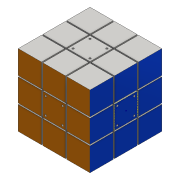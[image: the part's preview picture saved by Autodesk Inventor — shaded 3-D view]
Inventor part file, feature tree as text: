
AUTODESK INVENTOR PART (.ipt)
format: ipt  version: 2016 (Build 200138000, 138)  size: 400,384 bytes
history: native  units: mm
features: sketch x8, extrude x7, mirror x5, pattern_circular x5, plane x4, other x1, projected_geometry x1
ambient origin geometry x8: Origin, YZ Plane, XZ Plane, XY Plane, X Axis, Y Axis, Z Axis, Center Point
bodies: 实体1 (feature_tree)
feature tree (31):
  extrude  "拉伸1"  Depth=57.0mm TaperAngle=0.0deg
  extrude  "拉伸2"  Depth=1.0mm
  mirror  "镜像1"
  extrude  "拉伸3"  Depth=18.5mm
  plane  "工作平面1"
  mirror  "镜像2"
  pattern_circular  "环形阵列1"  Count=4 Angle=360.0deg
  pattern_circular  "环形阵列2"  Count=4 Angle=360.0deg
  extrude  "拉伸4"  Depth=1.0mm TaperAngle=360.0deg
  pattern_circular  "环形阵列3"  [2 undecoded]
  extrude  "拉伸5"  Depth=1.0mm
  mirror  "镜像3"
  extrude  "拉伸6"  Depth=18.5mm
  mirror  "镜像4"
  extrude  "拉伸7"  Depth=4.0mm TaperAngle=0.0deg
  mirror  "镜像5"
  pattern_circular  "环形阵列4"  [2 undecoded]
  sketch  "草图8"  dims[d23=1.0mm d24=18.5mm d25=1.0mm d26=18.5mm d27=60.0mm d28=0.0mm d29=1.0mm d30=0.0mm d31=19.0mm d32=1.5mm d33=1.5mm d34=4.0mm d35=0.0mm d36=40.0mm d37=360.0deg d39=40.0mm d40=360.0deg]
  other  "工作轴4"
  pattern_circular  "环形阵列5"  [2 undecoded]
  sketch  "草图1"  dims[d0=57.0mm d1=57.0mm d2=0.0mm]
  sketch  "草图2"  dims[d3=18.5mm d4=1.0mm]
  projected_geometry  "投影回路1"
  sketch  "草图3"  dims[d5=1.0mm d6=18.5mm]
  sketch  "草图4"  dims[d7=1.0mm d8=0.0mm]
  sketch  "草图5"  dims[d9=1.0mm d10=0.0mm]
  plane  "工作平面2"
  sketch  "草图6"  dims[d11=28.5mm d12=40.0mm d13=360.0deg d15=40.0mm d16=360.0deg]
  plane  "工作平面3"
  sketch  "草图7"  dims[d18=1.0mm d19=0.0mm d20=40.0mm d21=360.0deg]
  plane  "工作平面4"
note: 6 required parameter values undecoded (feature->parameter linkage not recoverable at this tier; creation-order binding heuristic only, values carry confidence <= 0.55)
